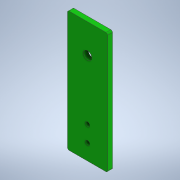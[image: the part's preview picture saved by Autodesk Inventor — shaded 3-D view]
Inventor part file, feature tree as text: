
AUTODESK INVENTOR PART (.ipt)
format: ipt  version: 2022 (Build 260153000, 153)  size: 123,904 bytes
history: native  units: mm
features: sketch x3, hole x2, extrude x1, fillet x1
ambient origin geometry x8: Origin, YZ Plane, XZ Plane, XY Plane, X Axis, Y Axis, Z Axis, Center Point
bodies: Solid1 (feature_tree)
feature tree (7):
  extrude  "Extrusion1"  Depth=150.0mm
  fillet  "Fillet1"  Radius=6.0mm
  hole  "Hole1"  [1 undecoded]
  hole  "Hole2"  [1 undecoded]
  sketch  "Sketch2"  dims[d0=50.0mm d1=150.0mm d2=6.0mm d3=0.0mm]
  sketch  "Sketch3"  dims[d4=2.0mm d5=36.4mm]
  sketch  "Sketch4"  dims[d6=10.5mm d7=6.0mm d8=4.0mm d9=2.0mm d10=90.0deg d11=8.0mm d12=20.594885mm d13=20.0mm d14=39.551mm d15=5.4mm d16=6.0mm d17=4.0mm d18=2.0mm d19=90.0deg d20=8.0mm d21=20.594885mm]
note: 2 required parameter values undecoded (feature->parameter linkage not recoverable at this tier; creation-order binding heuristic only, values carry confidence <= 0.55)
